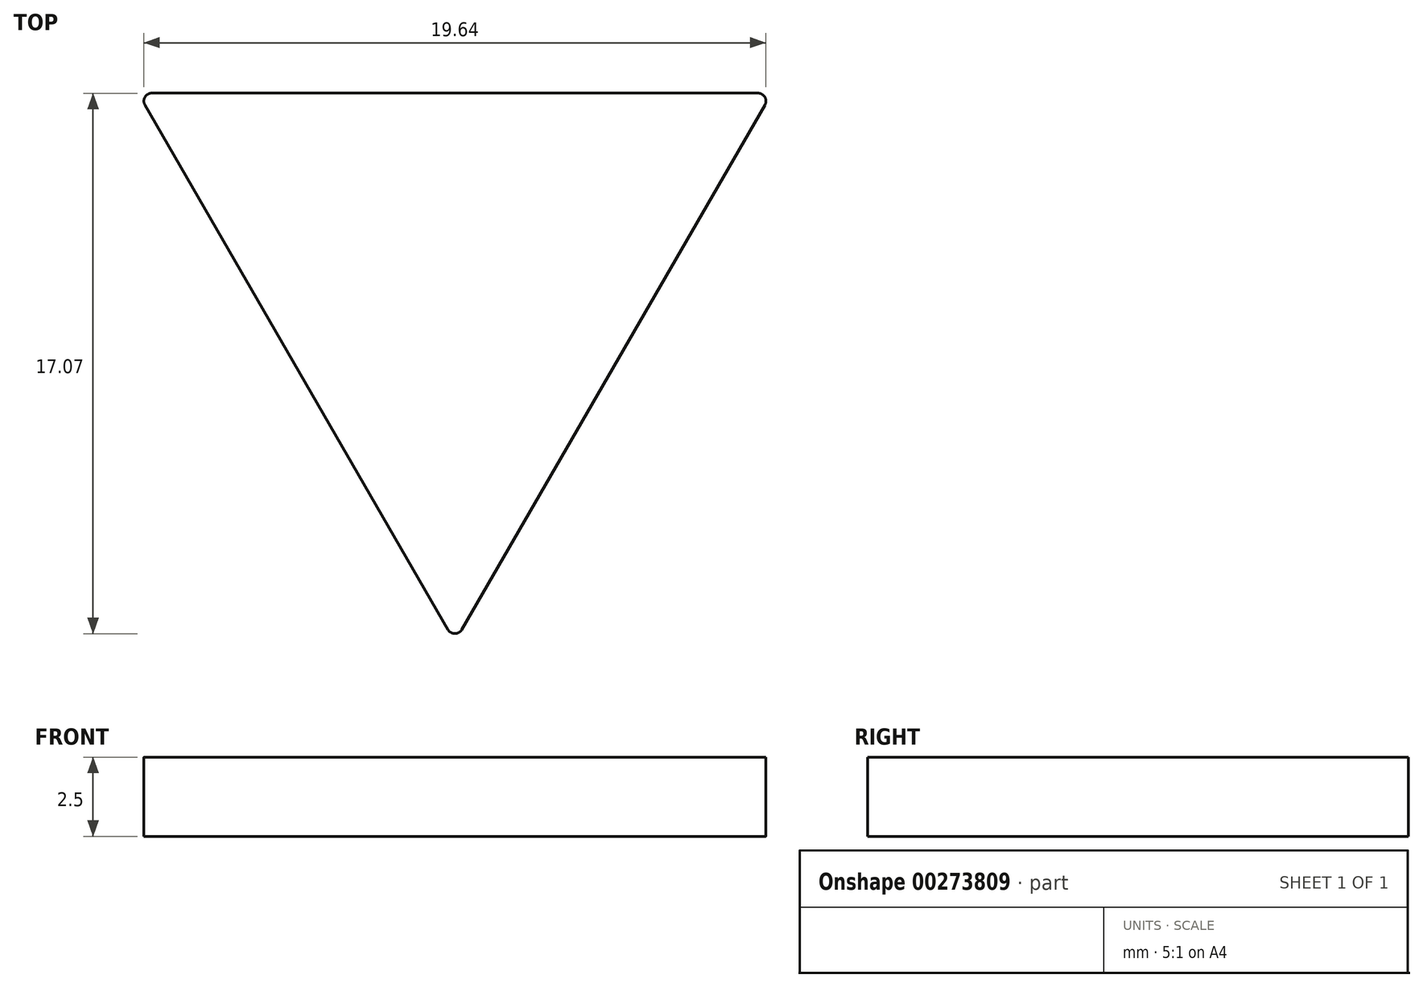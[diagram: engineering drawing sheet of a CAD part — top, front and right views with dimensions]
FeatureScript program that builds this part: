
annotation { "Feature Type Name" : "Feature", "Feature Type Description" : "" }
export const myFeature = defineFeature(function(context is Context, id is Id, definition is map)
    precondition{}
    {
        {
            var Q0;
            Q0=qCreatedBy(makeId("Top.planeOp"),FACE);
            var sketch = newSketch(context, id + "F0", { "sketchPlane" : qUnion([Q0])});
            skCircle(sketch, "E0.cCircle", {"center": v(0, 0) * mm, "radius": 11.55 * mm, "construction": true});
            skLineSegment(sketch, "E0.0", {"start": v(0, -11.55) * mm, "end": v(-10, 5.77) * mm});
            skLineSegment(sketch, "E0.1", {"start": v(-10, 5.77) * mm, "end": v(10, 5.77) * mm});
            skLineSegment(sketch, "E0.2", {"start": v(10, 5.77) * mm, "end": v(0, -11.55) * mm});
            skSolve(sketch);
        }
        {
            var Q0;
            Q0=makeQuery(id+"F0.imprint","IMPRINT",FACE,{"disambiguationData":[TD([[makeQuery(id+"F0.imprint","IMPRINT",EDGE,{"derivedFrom":sQuery(id+"F0.wireOp",EDGE,"E0.0")}),-1.0]])]});
            extrude(context, id + "F1", {"entities" : qUnion([Q0]), "depth" : 2.5 * mm, "offsetDistance" : 25 * mm});
        }
        {
            var Q0;
            Q0=makeQuery(id+"F1.opExtrude","SWEPT_EDGE",EDGE,{"disambiguationData":[OSD([sQuery(id+"F0.wireOp",EDGE,"E0.0"),sQuery(id+"F0.wireOp",EDGE,"E0.2")])]});
            var Q1;
            Q1=makeQuery(id+"F1.opExtrude","SWEPT_EDGE",EDGE,{"disambiguationData":[OSD([sQuery(id+"F0.wireOp",EDGE,"E0.1"),sQuery(id+"F0.wireOp",EDGE,"E0.2")])]});
            var Q2;
            Q2=makeQuery(id+"F1.opExtrude","SWEPT_EDGE",EDGE,{"disambiguationData":[OSD([sQuery(id+"F0.wireOp",EDGE,"E0.0"),sQuery(id+"F0.wireOp",EDGE,"E0.1")])]});
            fillet(context, id + "F2", {"entities" : qUnion([Q0, Q1, Q2]), "tangentPropagation" : true, "radius" : 0.25 * mm, "defaultsChanged" : true, "vertexSettings" : [], "allowEdgeOverflow" : false});
        }
    });
